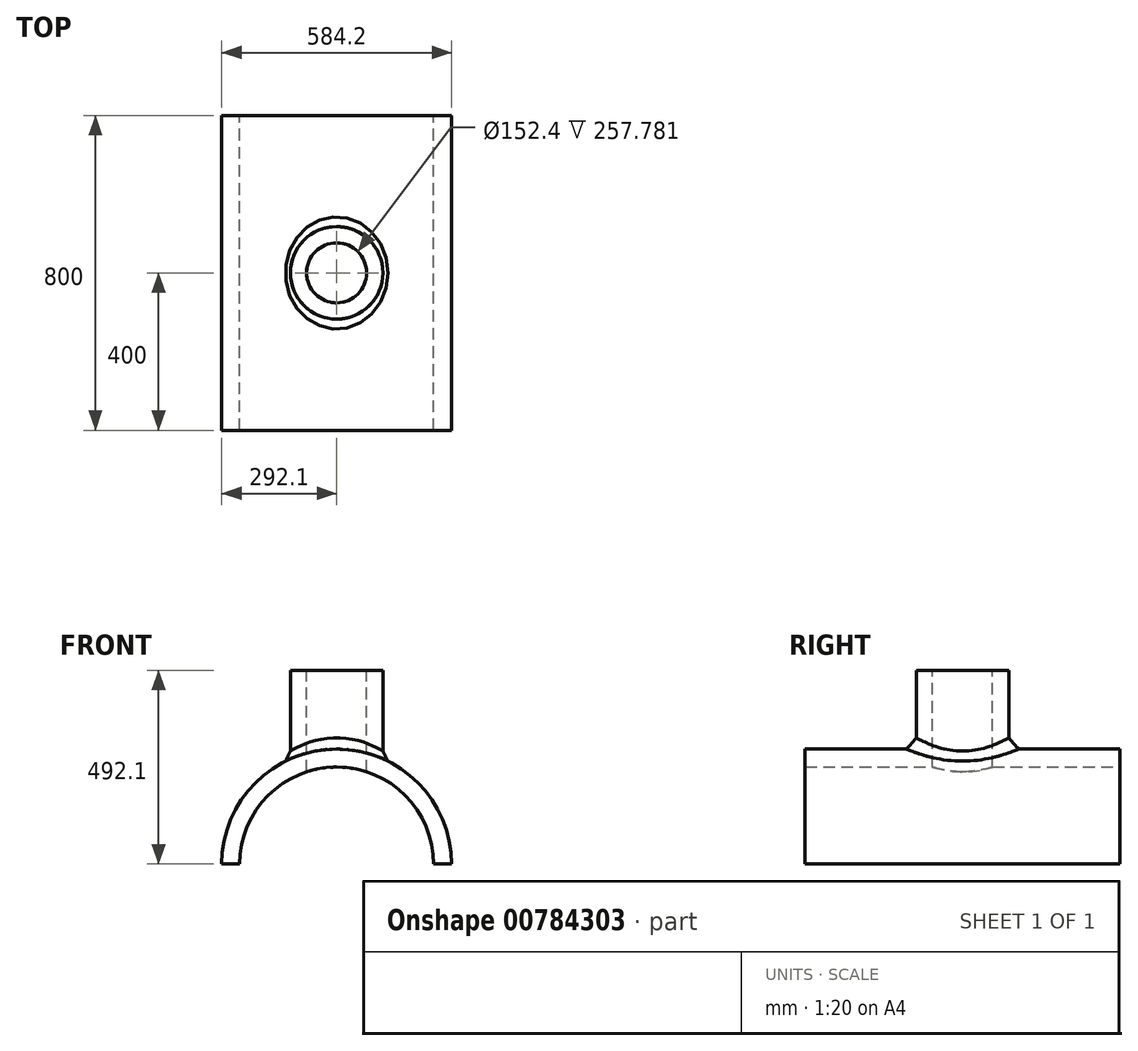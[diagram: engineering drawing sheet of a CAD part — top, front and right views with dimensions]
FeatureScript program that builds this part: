
annotation { "Feature Type Name" : "Feature", "Feature Type Description" : "" }
export const myFeature = defineFeature(function(context is Context, id is Id, definition is map)
    precondition{}
    {
        {
            var Q0;
            Q0=qCreatedBy(makeId("Front.planeOp"),FACE);
            var sketch = newSketch(context, id + "F0", { "sketchPlane" : qUnion([Q0])});
            skArc(sketch, "E0", {"start": v(292.1, 0) * mm, "mid": v(0, 292.1) * mm, "end": v(-292.1, 0) * mm});
            skArc(sketch, "E1", {"start": v(246.4, 0) * mm, "mid": v(0, 246.4) * mm, "end": v(-246.4, 0) * mm});
            skLineSegment(sketch, "E2.trimOffspring", {"start": v(246.4, 0) * mm, "end": v(292.1, 0) * mm});
            skLineSegment(sketch, "E3", {"start": v(-292.1, 0) * mm, "end": v(-246.4, 0) * mm});
            skSolve(sketch);
        }
        {
            var Q0;
            Q0 = qSketchRegion(id + "F0", true);
            extrude(context, id + "F1", {"entities" : qUnion([Q0]), "endBound" : BoundingType.SYMMETRIC, "depth" : 800 * mm, "offsetDistance" : 25.4 * mm});
        }
        {
            var Q0;
            Q0=makeQuery(id+"F1.opExtrude","CAP_EDGE",EDGE,{"disambiguationData":[OSD([sQuery(id+"F0.wireOp",EDGE,"E0")])],"isStart":true});
            cPoint(context, id + "F2", {"entities" : qUnion([Q0]), "parameter" : 0.5});
        }
        {
            var Q0;
            Q0=qCreatedBy(makeId("Top.planeOp"),FACE);
            var Q1;
            Q1 = qCreatedBy(id + "F2" ,VERTEX);
            cPlane(context, id + "F3", {"entities" : qUnion([Q0, Q1]), "cplaneType" : CPlaneType.PLANE_POINT, "offset" : 25.4 * mm, "width" : 152.4 * mm, "height" : 152.4 * mm});
        }
        {
            var Q0;
            Q0=qCreatedBy(id+"F3.planeOp",FACE);
            cPlane(context, id + "F4", {"entities" : qUnion([Q0]), "cplaneType" : CPlaneType.OFFSET, "offset" : 200 * mm, "width" : 152.4 * mm, "height" : 152.4 * mm});
        }
        {
            var Q0;
            Q0=qCreatedBy(id+"F4.planeOp",FACE);
            var sketch = newSketch(context, id + "F5", { "sketchPlane" : qUnion([Q0])});
            skCircle(sketch, "E4", {"center": v(0, 0) * mm, "radius": 117.5 * mm});
            skCircle(sketch, "E5", {"center": v(0, 0) * mm, "radius": 76.2 * mm});
            skSolve(sketch);
        }
        {
            var Q0;
            Q0 = qSketchRegion(id + "F5", true);
            var Q1;
            Q1=makeQuery(id+"F1.opExtrude","SWEPT_FACE",FACE,{"disambiguationData":[OSD([sQuery(id+"F0.wireOp",EDGE,"E1")])]});
            extrude(context, id + "F6", {"entities" : qUnion([Q0]), "operationType" : NewBodyOperationType.ADD, "endBound" : BoundingType.UP_TO_SURFACE, "oppositeDirection" : true, "depth" : 129.54 * mm, "endBoundEntityFace" : qUnion([Q1]), "offsetDistance" : 25.4 * mm});
        }
        {
            var Q0;
            Q0=qCreatedBy(id+"F4.planeOp",FACE);
            var sketch = newSketch(context, id + "F7", { "sketchPlane" : qUnion([Q0])});
            skCircle(sketch, "E6", {"center": v(0, 0) * mm, "radius": 76.2 * mm});
            skSolve(sketch);
        }
        {
            var Q0;
            Q0 = qSketchRegion(id + "F7", true);
            extrude(context, id + "F8", {"entities" : qUnion([Q0]), "operationType" : NewBodyOperationType.REMOVE, "endBound" : BoundingType.THROUGH_ALL, "oppositeDirection" : true, "depth" : 25.4 * mm, "offsetDistance" : 25.4 * mm});
        }
        {
            var Q0;
            Q0=makeQuery(id+"F6.boolean.opBoolean","INTERSECT",EDGE,{"derivedFrom":[makeQuery(id+"F1.opExtrude","SWEPT_FACE",FACE,{"disambiguationData":[OSD([sQuery(id+"F0.wireOp",EDGE,"E0")])]}),makeQuery(id+"F6.opExtrude","SWEPT_FACE",FACE,{"disambiguationData":[OSD([sQuery(id+"F5.wireOp",EDGE,"E4")])]})]});
            chamfer(context, id + "F9", {"entities" : qUnion([Q0]), "chamferType" : ChamferType.TWO_OFFSETS, "width1" : 15 * mm, "oppositeDirection" : false, "width2" : 20 * mm, "tangentPropagation" : true});
        }
        {
            var Q0;
            Q0=qCreatedBy(makeId("Right.planeOp"),FACE);
            var sketch = newSketch(context, id + "F10", { "sketchPlane" : qUnion([Q0])});
            skLineSegment(sketch, "E7", {"start": v(0, 492.1) * mm, "end": v(0, 0) * mm});
            skSolve(sketch);
        }
    });
